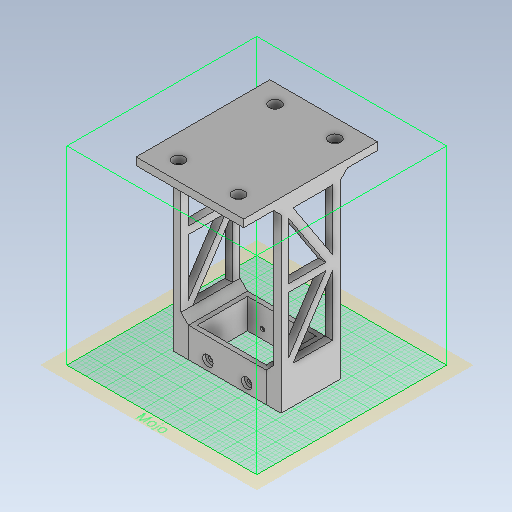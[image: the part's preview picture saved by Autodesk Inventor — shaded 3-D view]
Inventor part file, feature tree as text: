
AUTODESK INVENTOR PART (.ipt)
format: ipt  version: 2020 (Build 240168000, 168)  size: 539,136 bytes
history: native  units: mm
features: sketch x7, extrude x5, other x4, hole x2, mirror x2, projected_geometry x1
ambient origin geometry x8: Origin, YZ Plane, XZ Plane, XY Plane, X Axis, Y Axis, Z Axis, Center Point
bodies: Body1 (feature_tree), Body2 (feature_tree)
feature tree (21):
  other  "솔리드1"
  extrude  "돌출1"  Depth=46.0mm
  hole  "구멍1"  [1 undecoded]
  other  "작업 평면1"
  mirror  "미러1"
  extrude  "돌출3"  Depth=20.0mm TaperAngle=0.0deg
  extrude  "돌출4"  Depth=26.0mm
  other  "작업 평면2"
  mirror  "미러2"
  extrude  "돌출8"  Depth=13.0mm
  hole  "구멍4"  [1 undecoded]
  extrude  "돌출9"  Depth=5.0mm TaperAngle=0.0deg
  sketch  "스케치1"
  sketch  "스케치3"
  sketch  "스케치4"
  projected_geometry  "투영된 루프2"
  sketch  "스케치6"
  other  "솔리드2"
  sketch  "스케치12"
  sketch  "스케치13"
  sketch  "스케치14"
note: 2 required parameter values undecoded (feature->parameter linkage not recoverable at this tier; creation-order binding heuristic only, values carry confidence <= 0.55)
